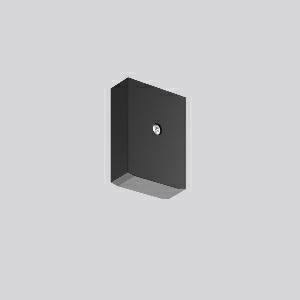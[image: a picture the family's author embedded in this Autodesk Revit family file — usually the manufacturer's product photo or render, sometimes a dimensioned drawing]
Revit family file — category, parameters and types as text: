
# Revit family: linedo_endkappe_b_f_982700_003_e18c
name_source: partatom
category: Lighting Fixtures
units: mm (PartAtom-declared; Revit-internal decimal feet)

## family parameters
Cut with Voids When Loaded = No
Host = Face
Light Source = No
Part Type = Normal
Room Calculation Point = No
Round Connector Dimension = Use Diameter
Shared = No

## types (1)
- LINEDO_Endkappe_B_F
    Apparent Load = 0 VA
    Default Elevation = 1800 mm
    Description = End cap low profile for LINEDO plug. Plastic end cap to cover the LINEDO plug system at the end of the line. Fastening by TX20 screw. Installation accessories included.
Colour: black
Length: 23 mm
Width: 58 mm
Height: 76 mm
Weight: 31 g
    Height = 76 mm
    Lamp = 0 x
    Length = 23 mm
    Luminous efficacy = 0 lm/W
    Manufacturer = RZB
    ModVariant = No
    Model = 982700.003
    Mounting Place = Ceiling
    Mounting Type = Surface mounted, Pendant
    Number of Poles = 1
    OnlyDefault = Yes
    Power Factor = 1
    Product Name = LINEDO_Endkappe_B_F
    Product group = Surface mounted continuous line luminaire system
    ProductGroupID = 310
    Protection Class = Protection class
    Protection Degree = Degree of protection
    RLX_Detail_Level = 1
    RLX_Emergency_Light_Flux = 0 lm
    RLX_Emergency_Type = 0
    RLX_Emergency_Type_DB = No
    RlxData = <blob elided: 10413 chars, md5=7c127a32>
    Standby Power = 0 W
    System Light Flux = 0 lm
    System Power = 0 W
    Type Comments = Product without accessories
    Type Image = 982700.003.jpg
    URL = http://relux.com
    VarID = ---
    Voltage = 0 V
    Weight = 0.00 kg
    Width = 58 mm

## geometry (parser evidence)
native form markers: Sweep x9
no freeform markers — native parametric forms only
